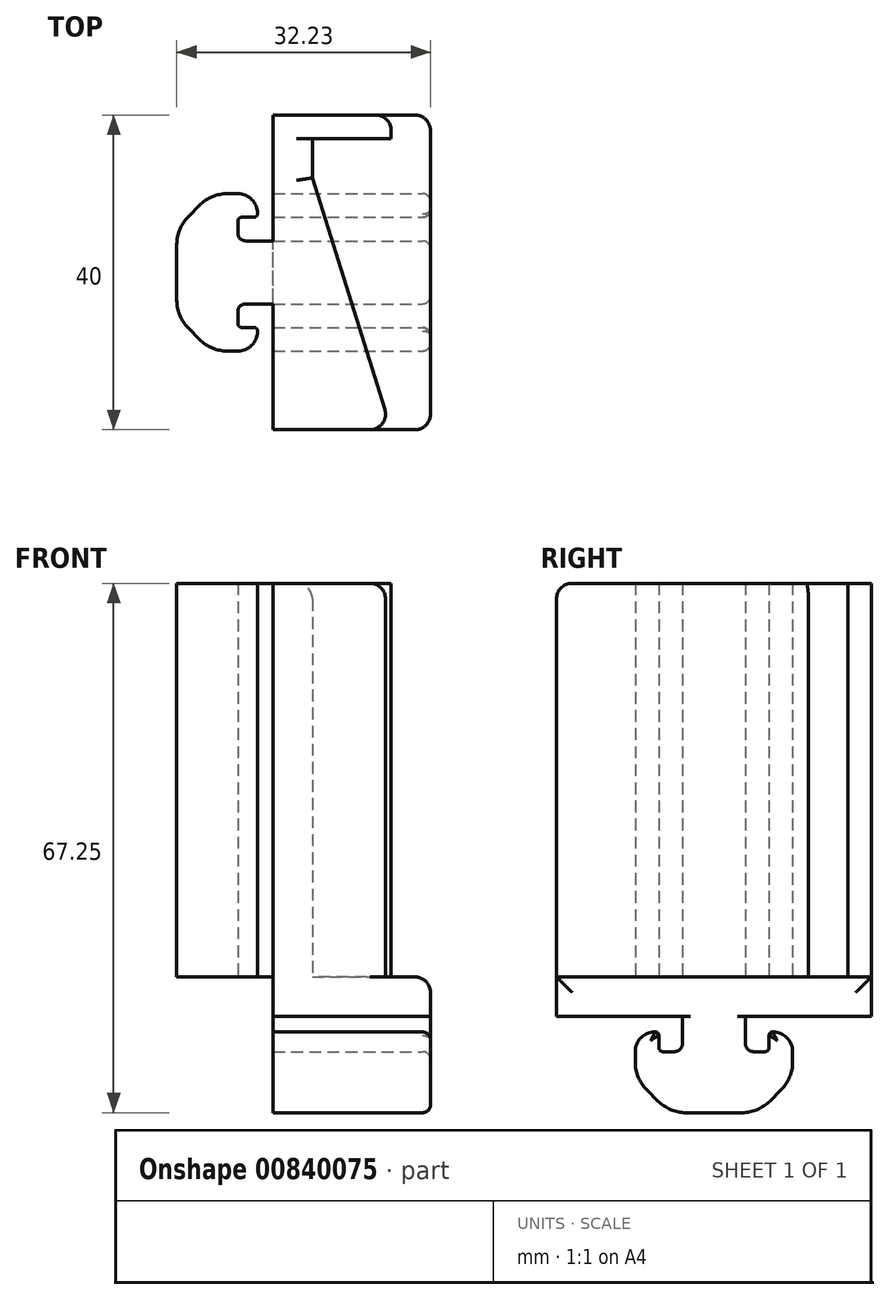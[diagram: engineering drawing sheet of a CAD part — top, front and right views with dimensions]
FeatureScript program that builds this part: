
annotation { "Feature Type Name" : "Feature", "Feature Type Description" : "" }
export const myFeature = defineFeature(function(context is Context, id is Id, definition is map)
    precondition{}
    {
        {
            var Q0;
            Q0=qCreatedBy(makeId("Top.planeOp"),FACE);
            var sketch = newSketch(context, id + "F0", { "sketchPlane" : qUnion([Q0])});
            skLineSegment(sketch, "E0", {"start": v(0, 0) * mm, "end": v(10, 0) * mm});
            skLineSegment(sketch, "E1", {"start": v(10, 0) * mm, "end": v(10, 3) * mm});
            skLineSegment(sketch, "E2", {"start": v(10, 3) * mm, "end": v(-5, 3) * mm});
            skLineSegment(sketch, "E3", {"start": v(-5, 3) * mm, "end": v(-5, -37) * mm});
            skLineSegment(sketch, "E4", {"start": v(-5, -37) * mm, "end": v(10, -37) * mm});
            skLineSegment(sketch, "E5", {"start": v(10, -37) * mm, "end": v(0, -5) * mm});
            skLineSegment(sketch, "E6", {"start": v(0, -5) * mm, "end": v(0, 0) * mm});
            skLineSegment(sketch, "E7", {"start": v(-4.98, -13) * mm, "end": v(-6.48, -13) * mm});
            skLineSegment(sketch, "E8", {"start": v(-6.48, -21) * mm, "end": v(-4.98, -21) * mm});
            skArc(sketch, "E9.0.62", {"start": v(-8.98, -37) * mm, "mid": v(-6.15, -35.83) * mm, "end": v(-4.98, -33) * mm, "construction": true});
            skLineSegment(sketch, "E9.0.63", {"start": v(-4.98, -33) * mm, "end": v(-4.98, -22.5) * mm, "construction": true});
            skArc(sketch, "E9.0.64", {"start": v(-4.98, -22.5) * mm, "mid": v(-5.42, -21.44) * mm, "end": v(-6.48, -21) * mm, "construction": true});
            skLineSegment(sketch, "E9.0.65", {"start": v(-6.48, -21) * mm, "end": v(-8.48, -21) * mm});
            skArc(sketch, "E9.0.66", {"start": v(-8.48, -21) * mm, "mid": v(-9.19, -21.3) * mm, "end": v(-9.48, -22) * mm});
            skLineSegment(sketch, "E9.0.67", {"start": v(-9.48, -22) * mm, "end": v(-9.48, -23.5) * mm});
            skArc(sketch, "E9.0.68", {"start": v(-9.48, -23.5) * mm, "mid": v(-9.33, -23.85) * mm, "end": v(-8.98, -24) * mm});
            skLineSegment(sketch, "E9.0.69", {"start": v(-8.98, -24) * mm, "end": v(-7.43, -24) * mm});
            skArc(sketch, "E9.0.70", {"start": v(-7.43, -24) * mm, "mid": v(-7.11, -24.13) * mm, "end": v(-6.98, -24.45) * mm});
            skLineSegment(sketch, "E9.0.71", {"start": v(-6.98, -24.45) * mm, "end": v(-6.98, -24.5) * mm});
            skArc(sketch, "E9.0.72", {"start": v(-6.98, -24.5) * mm, "mid": v(-7.71, -26.27) * mm, "end": v(-9.48, -27) * mm});
            skLineSegment(sketch, "E9.0.73", {"start": v(-9.48, -27) * mm, "end": v(-10.79, -27) * mm});
            skArc(sketch, "E9.0.74", {"start": v(-10.79, -27) * mm, "mid": v(-12.7, -26.62) * mm, "end": v(-14.32, -25.54) * mm});
            skLineSegment(sketch, "E9.0.75", {"start": v(-14.32, -25.54) * mm, "end": v(-15.76, -24.1) * mm});
            skArc(sketch, "E9.0.76", {"start": v(-15.76, -24.1) * mm, "mid": v(-16.85, -22.47) * mm, "end": v(-17.23, -20.56) * mm});
            skLineSegment(sketch, "E9.0.77", {"start": v(-17.23, -20.56) * mm, "end": v(-17.23, -13.44) * mm});
            skArc(sketch, "E9.0.78", {"start": v(-17.23, -13.44) * mm, "mid": v(-16.85, -11.53) * mm, "end": v(-15.76, -9.9) * mm});
            skLineSegment(sketch, "E9.0.79", {"start": v(-15.76, -9.9) * mm, "end": v(-14.32, -8.46) * mm});
            skArc(sketch, "E9.0.80", {"start": v(-14.32, -8.46) * mm, "mid": v(-12.7, -7.38) * mm, "end": v(-10.79, -7) * mm});
            skLineSegment(sketch, "E9.0.81", {"start": v(-10.79, -7) * mm, "end": v(-9.48, -7) * mm});
            skArc(sketch, "E9.0.82", {"start": v(-9.48, -7) * mm, "mid": v(-7.71, -7.73) * mm, "end": v(-6.98, -9.5) * mm});
            skLineSegment(sketch, "E9.0.83", {"start": v(-6.98, -9.5) * mm, "end": v(-6.98, -9.55) * mm});
            skArc(sketch, "E9.0.84", {"start": v(-6.98, -9.55) * mm, "mid": v(-7.11, -9.87) * mm, "end": v(-7.43, -10) * mm});
            skLineSegment(sketch, "E9.0.85", {"start": v(-7.43, -10) * mm, "end": v(-8.98, -10) * mm});
            skArc(sketch, "E9.0.86", {"start": v(-8.98, -10) * mm, "mid": v(-9.33, -10.15) * mm, "end": v(-9.48, -10.5) * mm});
            skLineSegment(sketch, "E9.0.87", {"start": v(-9.48, -10.5) * mm, "end": v(-9.48, -12) * mm});
            skArc(sketch, "E9.0.88", {"start": v(-9.48, -12) * mm, "mid": v(-9.19, -12.7) * mm, "end": v(-8.48, -13) * mm});
            skLineSegment(sketch, "E9.0.89", {"start": v(-8.48, -13) * mm, "end": v(-6.48, -13) * mm});
            skArc(sketch, "E9.0.90", {"start": v(-6.48, -13) * mm, "mid": v(-5.42, -12.56) * mm, "end": v(-4.98, -11.5) * mm, "construction": true});
            skLineSegment(sketch, "E9.0.91", {"start": v(-4.98, -11.5) * mm, "end": v(-4.98, -1) * mm, "construction": true});
            skArc(sketch, "E9.0.92", {"start": v(-4.98, -1) * mm, "mid": v(-6.15, 1.83) * mm, "end": v(-8.98, 3) * mm, "construction": true});
            skSolve(sketch);
        }
        {
            var Q0;
            Q0 = qSketchRegion(id + "F0", true);
            extrude(context, id + "F1", {"entities" : qUnion([Q0]), "depth" : 50 * mm, "offsetDistance" : 25 * mm});
        }
        {
            var Q0;
            Q0=qCreatedBy(makeId("Right.planeOp"),FACE);
            var sketch = newSketch(context, id + "F2", { "sketchPlane" : qUnion([Q0])});
            skLineSegment(sketch, "E10", {"start": v(3, 0) * mm, "end": v(-37, 0) * mm});
            skLineSegment(sketch, "E11", {"start": v(-37, 0) * mm, "end": v(-37, -5) * mm});
            skLineSegment(sketch, "E12", {"start": v(-37, -5) * mm, "end": v(-21, -5) * mm});
            skLineSegment(sketch, "E13", {"start": v(-21, -5) * mm, "end": v(-21, -6.5) * mm});
            skLineSegment(sketch, "E14", {"start": v(-13, -6.5) * mm, "end": v(-13, -5) * mm});
            skLineSegment(sketch, "E15", {"start": v(-13, -5) * mm, "end": v(3, -5) * mm});
            skLineSegment(sketch, "E16", {"start": v(3, -5) * mm, "end": v(3, 0) * mm});
            skArc(sketch, "E17.0.62", {"start": v(3, -9) * mm, "mid": v(1.83, -6.17) * mm, "end": v(-1, -5) * mm, "construction": true});
            skLineSegment(sketch, "E17.0.63", {"start": v(-1, -5) * mm, "end": v(-11.5, -5) * mm, "construction": true});
            skArc(sketch, "E17.0.64", {"start": v(-11.5, -5) * mm, "mid": v(-12.56, -5.44) * mm, "end": v(-13, -6.5) * mm, "construction": true});
            skLineSegment(sketch, "E17.0.65", {"start": v(-13, -6.5) * mm, "end": v(-13, -8.5) * mm});
            skArc(sketch, "E17.0.66", {"start": v(-13, -8.5) * mm, "mid": v(-12.7, -9.2) * mm, "end": v(-12, -9.5) * mm});
            skLineSegment(sketch, "E17.0.67", {"start": v(-12, -9.5) * mm, "end": v(-10.5, -9.5) * mm});
            skArc(sketch, "E17.0.68", {"start": v(-10.5, -9.5) * mm, "mid": v(-10.15, -9.35) * mm, "end": v(-10, -9) * mm});
            skLineSegment(sketch, "E17.0.69", {"start": v(-10, -9) * mm, "end": v(-10, -7.45) * mm});
            skArc(sketch, "E17.0.70", {"start": v(-10, -7.45) * mm, "mid": v(-9.87, -7.13) * mm, "end": v(-9.55, -7) * mm});
            skLineSegment(sketch, "E17.0.71", {"start": v(-9.55, -7) * mm, "end": v(-9.5, -7) * mm});
            skArc(sketch, "E17.0.72", {"start": v(-9.5, -7) * mm, "mid": v(-7.73, -7.73) * mm, "end": v(-7, -9.5) * mm});
            skLineSegment(sketch, "E17.0.73", {"start": v(-7, -9.5) * mm, "end": v(-7, -10.8) * mm});
            skArc(sketch, "E17.0.74", {"start": v(-7, -10.8) * mm, "mid": v(-7.38, -12.72) * mm, "end": v(-8.46, -14.34) * mm});
            skLineSegment(sketch, "E17.0.75", {"start": v(-8.46, -14.34) * mm, "end": v(-9.9, -15.79) * mm});
            skArc(sketch, "E17.0.76", {"start": v(-9.9, -15.79) * mm, "mid": v(-11.53, -16.87) * mm, "end": v(-13.44, -17.25) * mm});
            skLineSegment(sketch, "E17.0.77", {"start": v(-13.44, -17.25) * mm, "end": v(-20.56, -17.25) * mm});
            skArc(sketch, "E17.0.78", {"start": v(-20.56, -17.25) * mm, "mid": v(-22.47, -16.87) * mm, "end": v(-24.1, -15.79) * mm});
            skLineSegment(sketch, "E17.0.79", {"start": v(-24.1, -15.79) * mm, "end": v(-25.54, -14.34) * mm});
            skArc(sketch, "E17.0.80", {"start": v(-25.54, -14.34) * mm, "mid": v(-26.62, -12.72) * mm, "end": v(-27, -10.8) * mm});
            skLineSegment(sketch, "E17.0.81", {"start": v(-27, -10.8) * mm, "end": v(-27, -9.5) * mm});
            skArc(sketch, "E17.0.82", {"start": v(-27, -9.5) * mm, "mid": v(-26.27, -7.73) * mm, "end": v(-24.5, -7) * mm});
            skLineSegment(sketch, "E17.0.83", {"start": v(-24.5, -7) * mm, "end": v(-24.45, -7) * mm});
            skArc(sketch, "E17.0.84", {"start": v(-24.45, -7) * mm, "mid": v(-24.13, -7.13) * mm, "end": v(-24, -7.45) * mm});
            skLineSegment(sketch, "E17.0.85", {"start": v(-24, -7.45) * mm, "end": v(-24, -9) * mm});
            skArc(sketch, "E17.0.86", {"start": v(-24, -9) * mm, "mid": v(-23.85, -9.35) * mm, "end": v(-23.5, -9.5) * mm});
            skLineSegment(sketch, "E17.0.87", {"start": v(-23.5, -9.5) * mm, "end": v(-22, -9.5) * mm});
            skArc(sketch, "E17.0.88", {"start": v(-22, -9.5) * mm, "mid": v(-21.3, -9.2) * mm, "end": v(-21, -8.5) * mm});
            skLineSegment(sketch, "E17.0.89", {"start": v(-21, -8.5) * mm, "end": v(-21, -6.5) * mm});
            skArc(sketch, "E17.0.90", {"start": v(-21, -6.5) * mm, "mid": v(-21.44, -5.44) * mm, "end": v(-22.5, -5) * mm, "construction": true});
            skLineSegment(sketch, "E17.0.91", {"start": v(-22.5, -5) * mm, "end": v(-33, -5) * mm, "construction": true});
            skArc(sketch, "E17.0.92", {"start": v(-33, -5) * mm, "mid": v(-35.83, -6.17) * mm, "end": v(-37, -9) * mm, "construction": true});
            skSolve(sketch);
        }
        {
            var Q0;
            Q0 = qSketchRegion(id + "F2", true);
            var Q1;
            Q1=makeQuery(id+"F1.opExtrude","SWEPT_FACE",FACE,{"disambiguationData":[OSD([sQuery(id+"F0.wireOp",EDGE,"E3")])]});
            extrude(context, id + "F3", {"entities" : qUnion([Q0]), "operationType" : NewBodyOperationType.ADD, "endBound" : BoundingType.UP_TO_SURFACE, "oppositeDirection" : true, "depth" : 25 * mm, "endBoundEntityFace" : qUnion([Q1]), "offsetDistance" : 25 * mm});
        }
        {
            var Q0;
            Q0 = qSketchRegion(id + "F2", true);
            extrude(context, id + "F4", {"entities" : qUnion([Q0]), "operationType" : NewBodyOperationType.ADD, "depth" : 15 * mm, "offsetDistance" : 25 * mm});
        }
        {
            var Q0;
            Q0=makeQuery(id+"F1.opExtrude","SWEPT_EDGE",EDGE,{"disambiguationData":[OSD([sQuery(id+"F0.wireOp",EDGE,"E4"),sQuery(id+"F0.wireOp",EDGE,"E5")])]});
            var Q1;
            Q1=makeQuery(id+"F1.opExtrude","SWEPT_EDGE",EDGE,{"disambiguationData":[OSD([sQuery(id+"F0.wireOp",EDGE,"E1"),sQuery(id+"F0.wireOp",EDGE,"E2")])]});
            var Q2;
            Q2=makeQuery(id+"F4.opExtrude","CAP_EDGE",EDGE,{"disambiguationData":[OSD([sQuery(id+"F2.wireOp",EDGE,"E16")])],"isStart":false});
            var Q3;
            Q3=makeQuery(id+"F4.opExtrude","CAP_EDGE",EDGE,{"disambiguationData":[OSD([sQuery(id+"F2.wireOp",EDGE,"E10")])],"isStart":false});
            var Q4;
            Q4=makeQuery(id+"F4.opExtrude","CAP_EDGE",EDGE,{"disambiguationData":[OSD([sQuery(id+"F2.wireOp",EDGE,"E11")])],"isStart":false});
            var Q5;
            Q5=makeQuery(id+"F1.opExtrude","CAP_EDGE",EDGE,{"disambiguationData":[OSD([sQuery(id+"F0.wireOp",EDGE,"E4")])],"isStart":false});
            var Q6;
            Q6=makeQuery(id+"F1.opExtrude","CAP_EDGE",EDGE,{"disambiguationData":[OSD([sQuery(id+"F0.wireOp",EDGE,"E5")])],"isStart":false});
            var Q7;
            Q7=makeQuery(id+"F1.opExtrude","CAP_EDGE",EDGE,{"disambiguationData":[OSD([sQuery(id+"F0.wireOp",EDGE,"E6")])],"isStart":false});
            fillet(context, id + "F5", {"entities" : qUnion([Q0, Q1, Q2, Q3, Q4, Q5, Q6, Q7]), "radius" : 2 * mm, "tangentPropagation" : true, "allowEdgeOverflow" : false});
        }
        {
            var Q0;
            Q0=makeQuery(id+"F4.opExtrude","CAP_EDGE",EDGE,{"disambiguationData":[OSD([sQuery(id+"F2.wireOp",EDGE,"E17.0.87")])],"isStart":false});
            fillet(context, id + "F6", {"entities" : qUnion([Q0]), "radius" : 1 * mm, "tangentPropagation" : true, "allowEdgeOverflow" : false});
        }
    });
